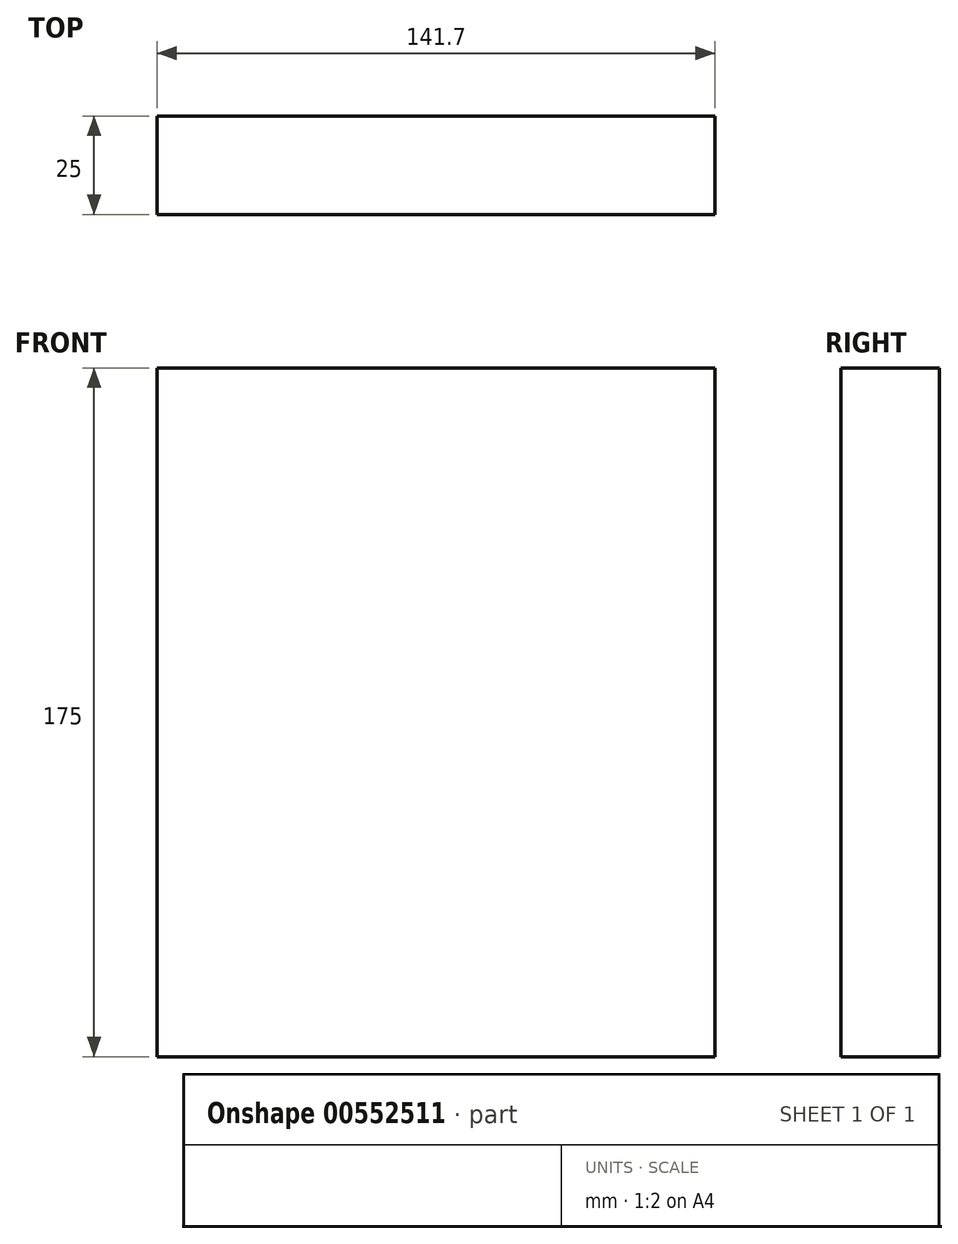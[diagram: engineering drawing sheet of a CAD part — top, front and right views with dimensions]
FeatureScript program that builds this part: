
annotation { "Feature Type Name" : "Feature", "Feature Type Description" : "" }
export const myFeature = defineFeature(function(context is Context, id is Id, definition is map)
    precondition{}
    {
        {
            var Q0;
            Q0=qCreatedBy(makeId("Front.planeOp"),FACE);
            var sketch = newSketch(context, id + "F0", { "sketchPlane" : qUnion([Q0])});
            skLineSegment(sketch, "E0.bottom", {"start": v(-70.85, 87.5) * mm, "end": v(70.85, 87.5) * mm});
            skLineSegment(sketch, "E0.top", {"start": v(-70.85, -87.5) * mm, "end": v(70.85, -87.5) * mm});
            skLineSegment(sketch, "E0.left", {"start": v(-70.85, 87.5) * mm, "end": v(-70.85, -87.5) * mm});
            skLineSegment(sketch, "E0.right", {"start": v(70.85, 87.5) * mm, "end": v(70.85, -87.5) * mm});
            skPoint(sketch, "E0.middle", {"position": v(0, 0) * mm});
            skLineSegment(sketch, "E1", {"start": v(-45.85, 37.5) * mm, "end": v(-70.85, 37.5) * mm});
            skLineSegment(sketch, "E2", {"start": v(-70.85, 37.5) * mm, "end": v(-45.85, 37.5) * mm});
            skLineSegment(sketch, "E3", {"start": v(-45.85, -37.5) * mm, "end": v(-45.85, 37.5) * mm});
            skLineSegment(sketch, "E4", {"start": v(-70.85, -37.5) * mm, "end": v(-45.85, -37.5) * mm});
            skLineSegment(sketch, "E5", {"start": v(-70.85, 37.5) * mm, "end": v(-70.85, 87.5) * mm});
            skLineSegment(sketch, "E6", {"start": v(-70.85, -87.5) * mm, "end": v(-70.85, -37.5) * mm});
            skLineSegment(sketch, "E7", {"start": v(70.85, 37.5) * mm, "end": v(70.85, 87.5) * mm});
            skLineSegment(sketch, "E8", {"start": v(45.85, 37.5) * mm, "end": v(70.85, 37.5) * mm});
            skLineSegment(sketch, "E9", {"start": v(45.85, -37.5) * mm, "end": v(45.85, 37.5) * mm});
            skLineSegment(sketch, "E10", {"start": v(70.85, -37.17) * mm, "end": v(45.85, -37.5) * mm});
            skSolve(sketch);
        }
        {
            var Q0;
            Q0 = qSketchRegion(id + "F0", true);
            extrude(context, id + "F1", {"entities" : qUnion([Q0]), "depth" : 25 * mm, "offsetDistance" : 25 * mm});
        }
        {
            var Q0;
            Q0 = qSketchRegion(id + "F0", true);
            extrude(context, id + "F2", {"entities" : qUnion([Q0]), "operationType" : NewBodyOperationType.ADD, "depth" : 25 * mm, "offsetDistance" : 25 * mm});
        }
    });
